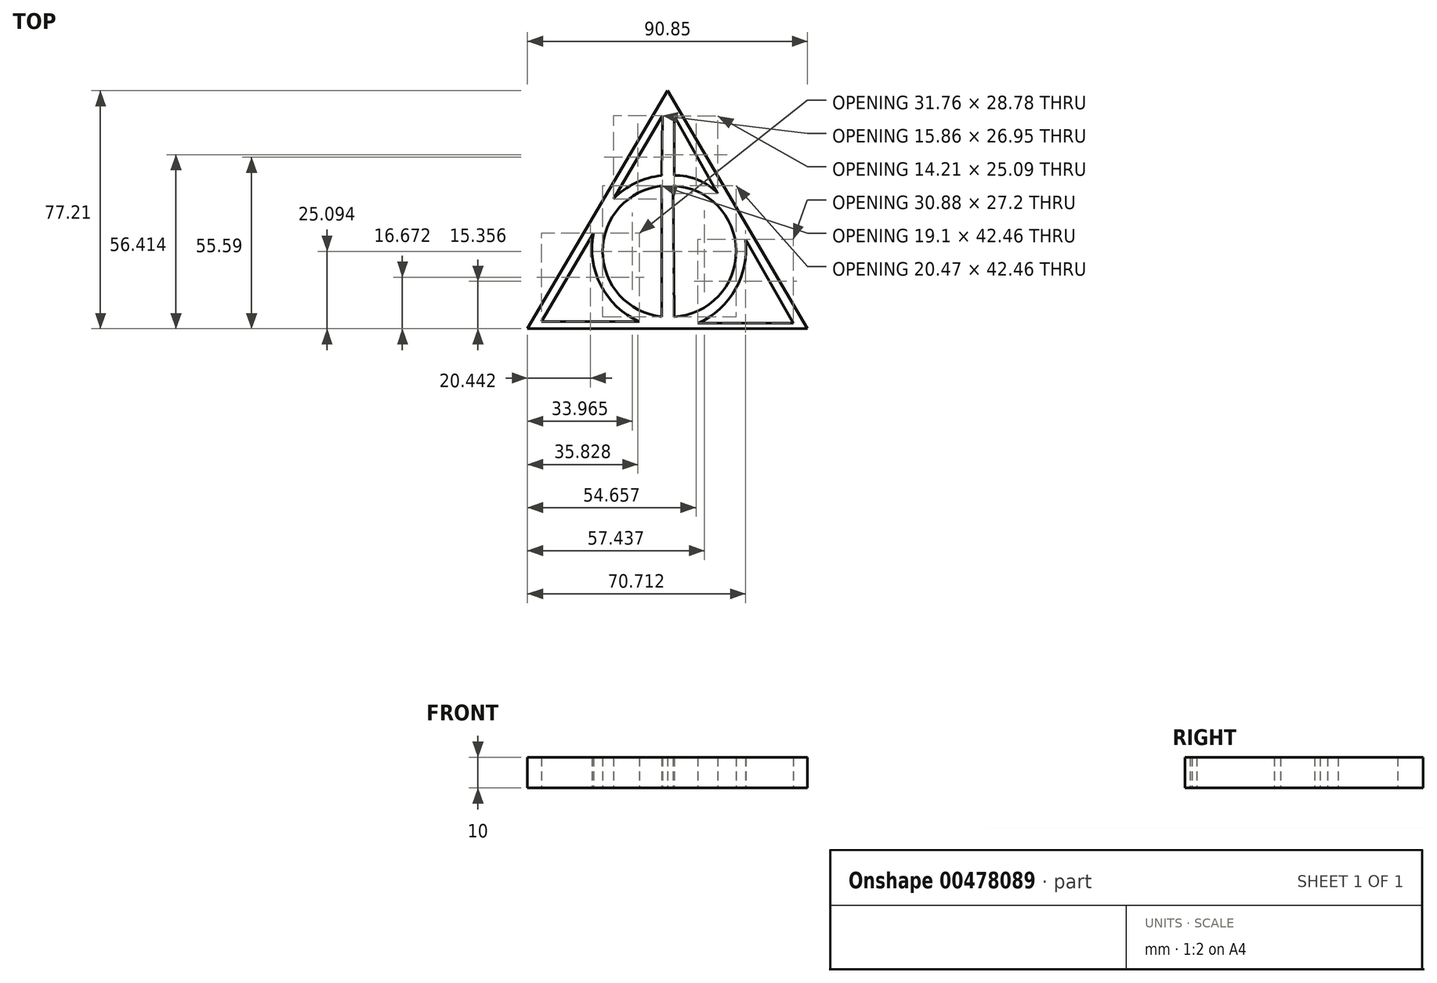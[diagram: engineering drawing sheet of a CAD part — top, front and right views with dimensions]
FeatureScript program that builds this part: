
annotation { "Feature Type Name" : "Feature", "Feature Type Description" : "" }
export const myFeature = defineFeature(function(context is Context, id is Id, definition is map)
    precondition{}
    {
        {
            var Q0;
            Q0=qCreatedBy(makeId("Top.planeOp"),FACE);
            var sketch = newSketch(context, id + "F0", { "sketchPlane" : qUnion([Q0])});
            skPoint(sketch, "E0.middle", {"position": v(0, 0) * mm});
            skLineSegment(sketch, "E1", {"start": v(0.15, 46.15) * mm, "end": v(-45.27, -31.06) * mm});
            skLineSegment(sketch, "E2", {"start": v(-45.27, -31.06) * mm, "end": v(45.58, -31.06) * mm});
            skLineSegment(sketch, "E3", {"start": v(45.58, -31.06) * mm, "end": v(0.15, 46.15) * mm});
            skLineSegment(sketch, "E4", {"start": v(-40.7, -28.78) * mm, "end": v(-23.78, 0) * mm});
            skLineSegment(sketch, "E5", {"start": v(-40.7, -28.78) * mm, "end": v(-8.95, -28.78) * mm});
            skArc(sketch, "E6", {"start": v(-23.78, 0) * mm, "mid": v(-21.46, -17.01) * mm, "end": v(-8.95, -28.78) * mm});
            skArc(sketch, "E7", {"start": v(-1.75, 18.6) * mm, "mid": v(-10.23, 16.2) * mm, "end": v(-17.37, 11.05) * mm});
            skArc(sketch, "E8", {"start": v(16.5, 12.8) * mm, "mid": v(10, 17.22) * mm, "end": v(2.28, 18.6) * mm});
            skArc(sketch, "E9", {"start": v(10, -29.3) * mm, "mid": v(22.2, -18.24) * mm, "end": v(25.44, -2.1) * mm});
            skArc(sketch, "E10", {"start": v(2.28, -27.2) * mm, "mid": v(22.4, -5.8) * mm, "end": v(1.93, 15.27) * mm});
            skArc(sketch, "E11", {"start": v(-1.75, 15.27) * mm, "mid": v(-20.86, -5.97) * mm, "end": v(-1.75, -27.2) * mm});
            skLineSegment(sketch, "E12", {"start": v(-17.37, 11.05) * mm, "end": v(-1.51, 38) * mm});
            skLineSegment(sketch, "E13", {"start": v(-1.51, 38) * mm, "end": v(-1.75, 18.6) * mm});
            skLineSegment(sketch, "E14", {"start": v(2.28, 18.6) * mm, "end": v(2.28, 37.9) * mm});
            skLineSegment(sketch, "E15", {"start": v(2.28, 37.9) * mm, "end": v(16.5, 12.8) * mm});
            skLineSegment(sketch, "E16", {"start": v(10, -29.3) * mm, "end": v(40.88, -29.3) * mm});
            skLineSegment(sketch, "E17", {"start": v(40.88, -29.3) * mm, "end": v(25.44, -2.1) * mm});
            skLineSegment(sketch, "E18", {"start": v(1.93, 15.27) * mm, "end": v(2.28, -27.2) * mm});
            skLineSegment(sketch, "E19", {"start": v(-1.75, -27.2) * mm, "end": v(-1.75, 15.27) * mm});
            skSolve(sketch);
        }
        {
            var Q0;
            Q0 = qSketchRegion(id + "F0", true);
            extrude(context, id + "F1", {"entities" : qUnion([Q0]), "depth" : 10 * mm});
        }
    });
